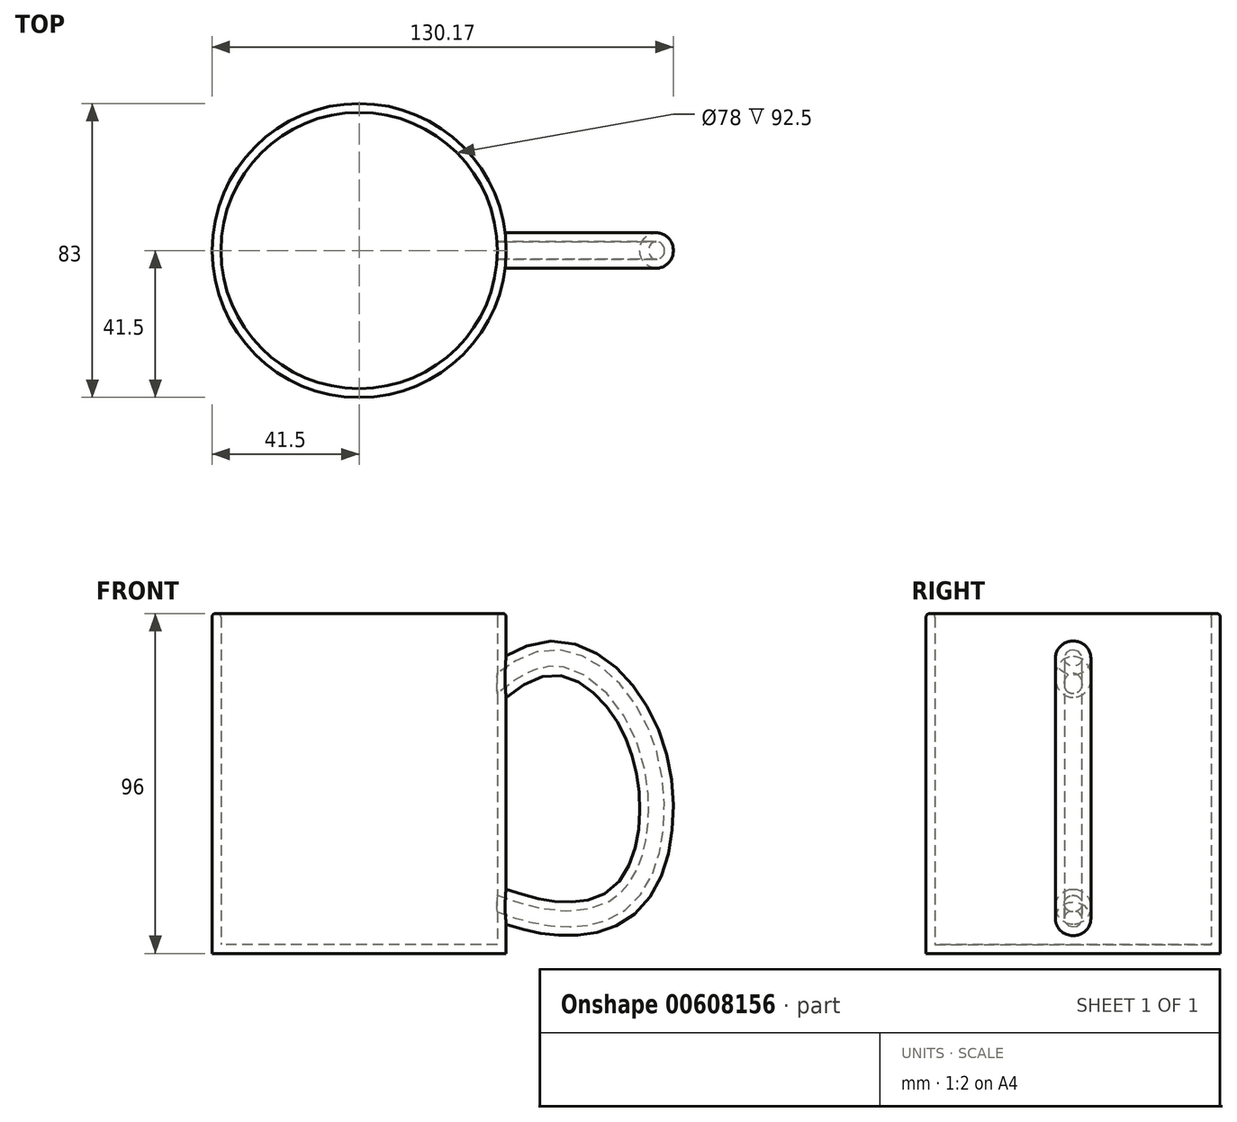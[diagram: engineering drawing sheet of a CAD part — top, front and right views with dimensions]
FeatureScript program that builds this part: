
annotation { "Feature Type Name" : "Feature", "Feature Type Description" : "" }
export const myFeature = defineFeature(function(context is Context, id is Id, definition is map)
    precondition{}
    {
        {
            var Q0;
            Q0=qCreatedBy(makeId("Top.planeOp"),FACE);
            var sketch = newSketch(context, id + "F0", { "sketchPlane" : qUnion([Q0])});
            skCircle(sketch, "E0", {"center": v(0, 0) * mm, "radius": 41.5 * mm});
            skSolve(sketch);
        }
        {
            var Q0;
            Q0 = qSketchRegion(id + "F0", true);
            extrude(context, id + "F1", {"entities" : qUnion([Q0]), "depth" : 96 * mm, "offsetDistance" : 25 * mm});
        }
        {
            var Q0;
            Q0=qCreatedBy(makeId("Front.planeOp"),FACE);
            var sketch = newSketch(context, id + "F2", { "sketchPlane" : qUnion([Q0])});
            skFitSpline(sketch, "E1", {"points": [v(30.58, 63) * mm, v(55.32, 79.72) * mm, v(77.38, 58.33) * mm, v(74.7, 20.22) * mm, v(55.99, 13.54) * mm, v(32.26, 20.56) * mm], "startDerivative": vector(118.39, 123.9) * mm, "endDerivative": vector(-126.9, 51) * mm});
            skSolve(sketch);
        }
        {
            var Q0;
            Q0=qCreatedBy(makeId("Right.planeOp"),FACE);
            cPlane(context, id + "F3", {"entities" : qUnion([Q0]), "cplaneType" : CPlaneType.OFFSET, "offset" : 40 * mm, "width" : 150 * mm, "height" : 150 * mm});
        }
        {
            var Q0;
            Q0=qCreatedBy(id+"F3.planeOp",FACE);
            var sketch = newSketch(context, id + "F4", { "sketchPlane" : qUnion([Q0])});
            skCircle(sketch, "E2", {"center": v(0, 13.7) * mm, "radius": 5 * mm});
            skSolve(sketch);
        }
        {
            var Q0;
            Q0 = qSketchRegion(id + "F4", true);
            var Q1;
            Q1=sQuery(id+"F2.wireOp",EDGE,"E1");
            sweep(context, id + "F5", {"operationType" : NewBodyOperationType.ADD, "profiles" : qUnion([Q0]), "path" : qUnion([Q1])});
        }
        {
            var Q0;
            Q0=makeQuery(id+"F1.opExtrude","CAP_FACE",FACE,{"disambiguationData":[OSD([sQuery(id+"F0.wireOp",EDGE,"E0")])],"isStart":false});
            shell(context, id + "F6", {"entities" : qUnion([Q0]), "thickness" : 2.5 * mm});
        }
        {
            var Q0;
            Q0=makeQuery(id+"F1.opExtrude","CAP_EDGE",EDGE,{"disambiguationData":[OSD([sQuery(id+"F0.wireOp",EDGE,"E0")])],"isStart":false});
            var Q1;
            {var subQ0=sQuery(id+"F0.wireOp",EDGE,"E0");Q1=makeQuery(id+"F6.opShell","OFFSET_EDGE",EDGE,{"disambiguationData":[OSD([subQ0]),TDD([makeQuery(id+"F1.opExtrude","CAP_EDGE",EDGE,{"disambiguationData":[OSD([subQ0])],"isStart":false})])]});}
            fillet(context, id + "F7", {"entities" : qUnion([Q0, Q1]), "radius" : 1 * mm, "tangentPropagation" : true, "allowEdgeOverflow" : false});
        }
    });
